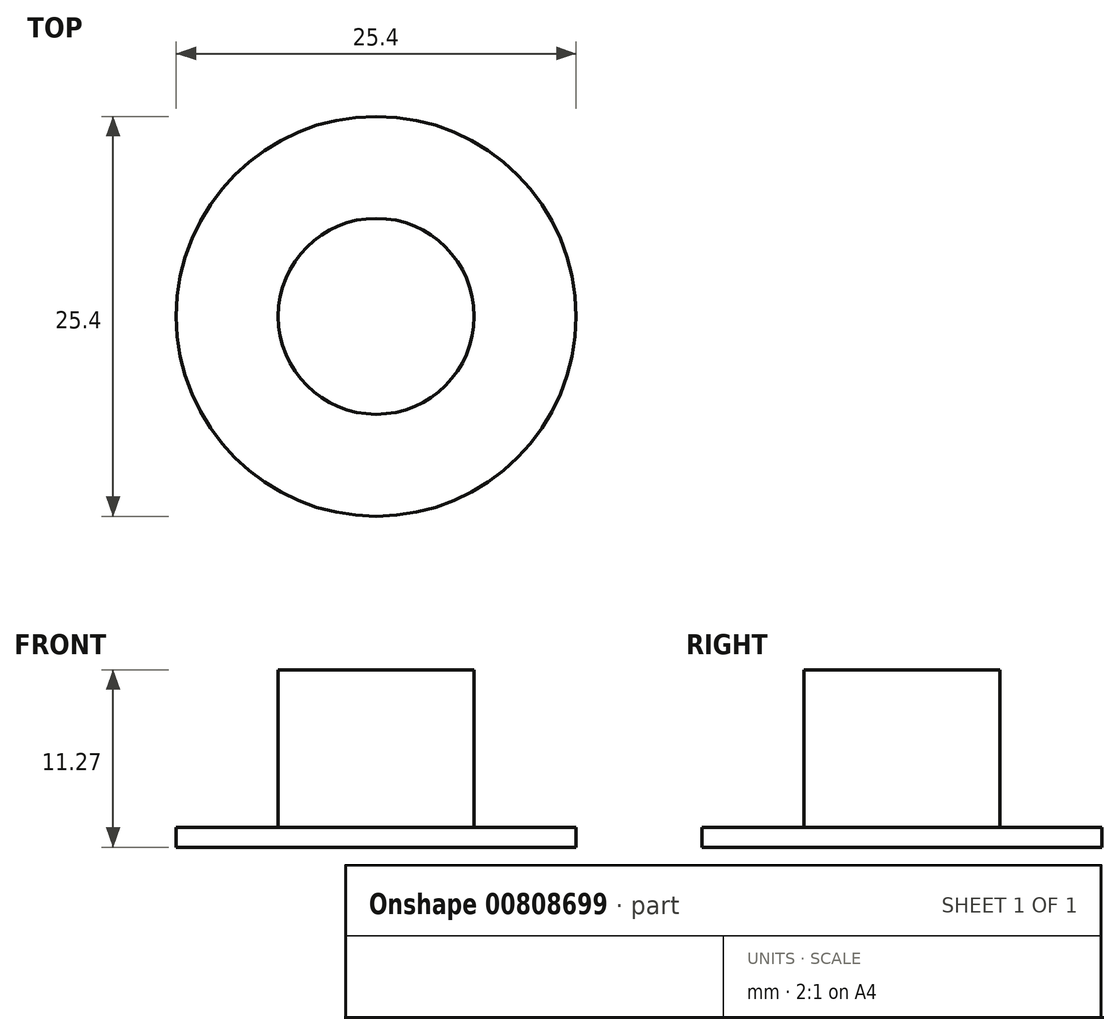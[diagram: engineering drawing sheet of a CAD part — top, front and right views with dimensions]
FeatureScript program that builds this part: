
annotation { "Feature Type Name" : "Feature", "Feature Type Description" : "" }
export const myFeature = defineFeature(function(context is Context, id is Id, definition is map)
    precondition{}
    {
        {
            var Q0;
            Q0=qCreatedBy(makeId("Top.planeOp"),FACE);
            var sketch = newSketch(context, id + "F0", { "sketchPlane" : qUnion([Q0])});
            skCircle(sketch, "E0", {"center": v(0, 0) * mm, "radius": 12.7 * mm});
            skSolve(sketch);
        }
        {
            var Q0;
            Q0 = qSketchRegion(id + "F0", true);
            extrude(context, id + "F1", {"entities" : qUnion([Q0]), "depth" : 1.27 * mm, "offsetDistance" : 25.4 * mm});
        }
        {
            var Q0;
            Q0=makeQuery(id+"F1.opExtrude","CAP_FACE",FACE,{"disambiguationData":[OSD([sQuery(id+"F0.wireOp",EDGE,"E0")])],"isStart":false});
            var sketch = newSketch(context, id + "F2", { "sketchPlane" : qUnion([Q0])});
            skCircle(sketch, "E1", {"center": v(0, 0) * mm, "radius": 6.22 * mm});
            skSolve(sketch);
        }
        {
            var Q0;
            Q0=makeQuery(id+"F2.imprint","IMPRINT",FACE,{"disambiguationData":[TD([[makeQuery(id+"F2.imprint","IMPRINT",EDGE,{"derivedFrom":sQuery(id+"F2.wireOp",EDGE,"E1")}),1.0]])]});
            extrude(context, id + "F3", {"entities" : qUnion([Q0]), "depth" : 10 * mm, "offsetDistance" : 25.4 * mm});
        }
    });
